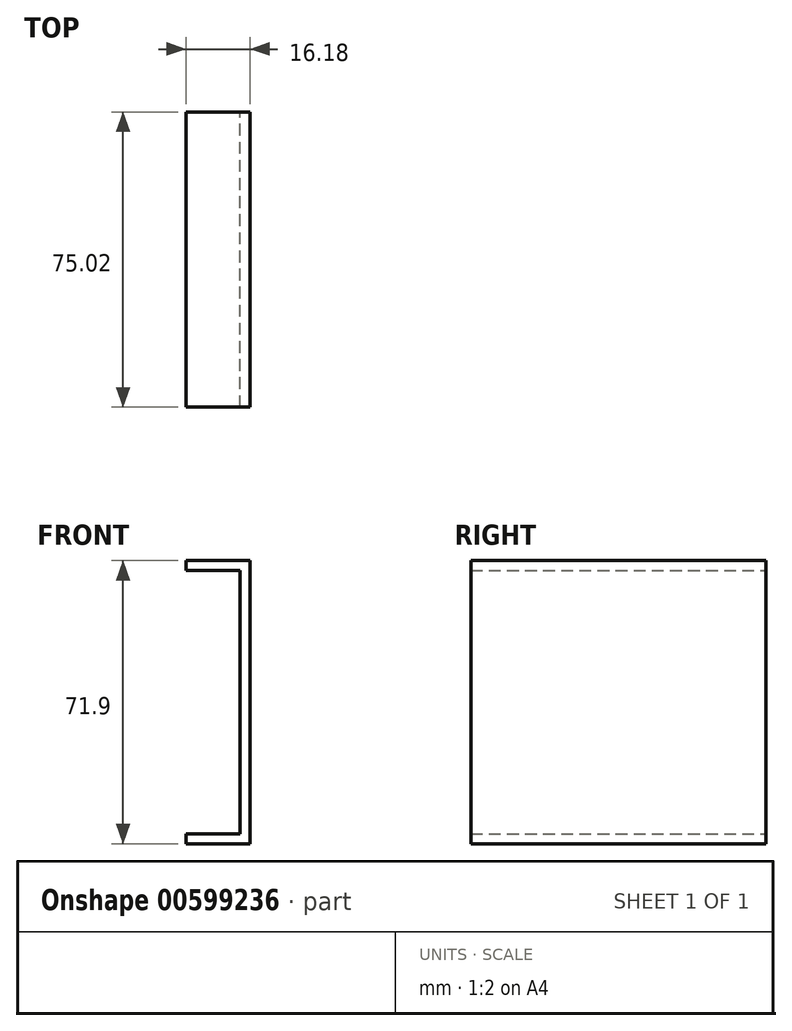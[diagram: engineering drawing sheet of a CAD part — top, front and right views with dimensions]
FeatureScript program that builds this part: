
annotation { "Feature Type Name" : "Feature", "Feature Type Description" : "" }
export const myFeature = defineFeature(function(context is Context, id is Id, definition is map)
    precondition{}
    {
        {
            var Q0;
            Q0=qCreatedBy(makeId("Right.planeOp"),FACE);
            var sketch = newSketch(context, id + "F0", { "sketchPlane" : qUnion([Q0])});
            skLineSegment(sketch, "E0.bottom", {"start": v(-37.5, -35.95) * mm, "end": v(37.5, -35.95) * mm});
            skLineSegment(sketch, "E0.top", {"start": v(-37.5, 35.95) * mm, "end": v(37.5, 35.95) * mm});
            skLineSegment(sketch, "E0.left", {"start": v(-37.5, -35.95) * mm, "end": v(-37.5, 35.95) * mm});
            skLineSegment(sketch, "E0.right", {"start": v(37.5, -35.95) * mm, "end": v(37.5, 35.95) * mm});
            skPoint(sketch, "E0.middle", {"position": v(0, 0) * mm});
            skSolve(sketch);
        }
        {
            var Q0;
            Q0 = qSketchRegion(id + "F0", true);
            extrude(context, id + "F1", {"entities" : qUnion([Q0]), "depth" : 16.18 * mm, "offsetDistance" : 25.4 * mm});
        }
        {
            var Q0;
            Q0=makeQuery(id+"F1.opExtrude","CAP_FACE",FACE,{"disambiguationData":[OSD([sQuery(id+"F0.wireOp",EDGE,"E0.bottom"),sQuery(id+"F0.wireOp",EDGE,"E0.top"),sQuery(id+"F0.wireOp",EDGE,"E0.left"),sQuery(id+"F0.wireOp",EDGE,"E0.right")])],"isStart":true});
            var Q1;
            Q1=makeQuery(id+"F1.opExtrude","SWEPT_FACE",FACE,{"disambiguationData":[OSD([sQuery(id+"F0.wireOp",EDGE,"E0.left")])]});
            var Q2;
            Q2=makeQuery(id+"F1.opExtrude","SWEPT_FACE",FACE,{"disambiguationData":[OSD([sQuery(id+"F0.wireOp",EDGE,"E0.right")])]});
            shell(context, id + "F2", {"entities" : qUnion([Q0, Q1, Q2]), "thickness" : 2.54 * mm});
        }
    });
